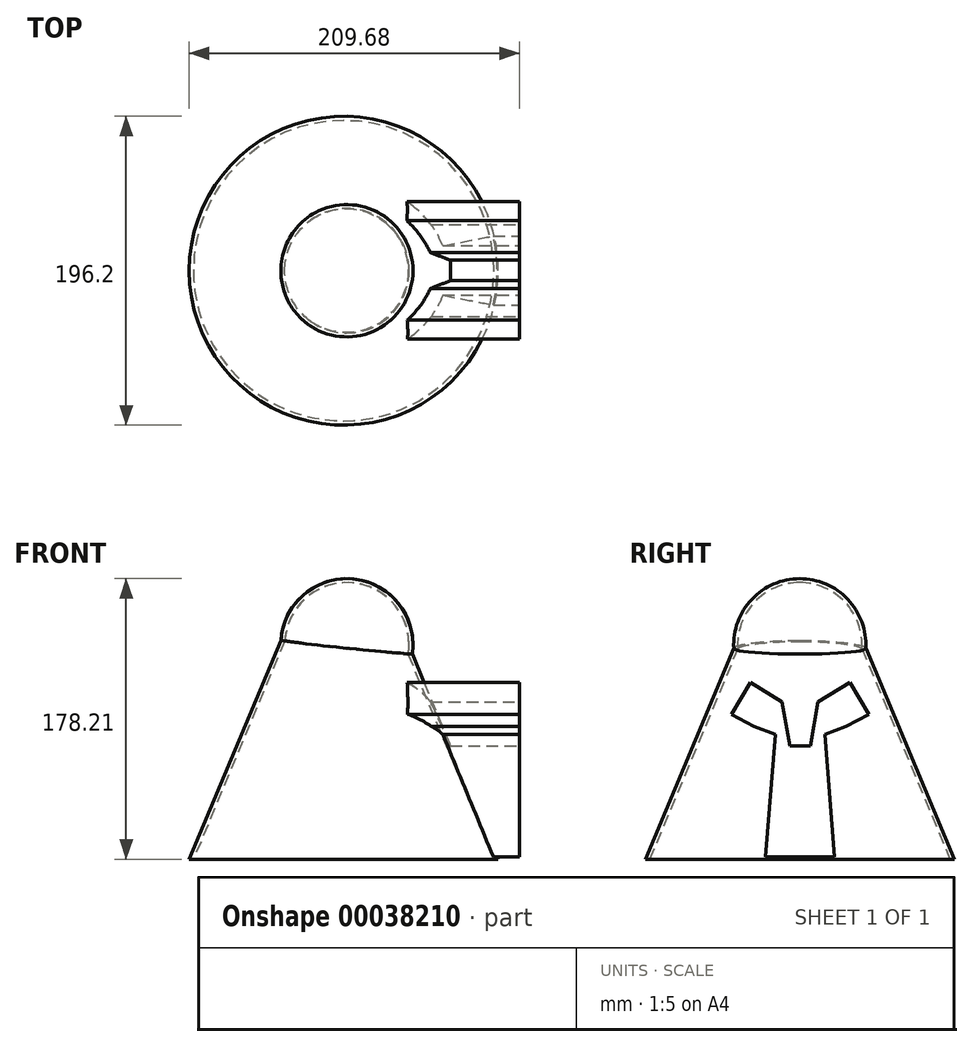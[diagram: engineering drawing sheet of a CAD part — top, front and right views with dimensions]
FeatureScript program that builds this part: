
annotation { "Feature Type Name" : "Feature", "Feature Type Description" : "" }
export const myFeature = defineFeature(function(context is Context, id is Id, definition is map)
    precondition{}
    {
        {
            var Q0;
            Q0=qCreatedBy(makeId("Front.planeOp"),FACE);
            var sketch = newSketch(context, id + "F0", { "sketchPlane" : qUnion([Q0])});
            skLineSegment(sketch, "E0", {"start": v(-51.63, 23.51) * mm, "end": v(55.11, 23.51) * mm});
            skCircle(sketch, "E1", {"center": v(-9.58, 23.51) * mm, "radius": 42 * mm});
            skSolve(sketch);
        }
        {
            var Q0;
            {var subQ0=sQuery(id+"F0.wireOp",EDGE,"E1");var subQ1=sQuery(id+"F0.wireOp",EDGE,"E0");var subQ3=makeQuery(id+"F0.imprint","INTERSECT",VERTEX,{"disambiguationData":[OD(0.0)],"derivedFrom":[subQ1,subQ0]});Q0=makeQuery(id+"F0.imprint","IMPRINT",FACE,{"disambiguationData":[TD([[makeQuery(id+"F0.imprint","IMPRINT",EDGE,{"disambiguationData":[TD([[subQ3,-1.0]])],"derivedFrom":subQ1}),1.0]])]});}
            var Q1;
            Q1=sQuery(id+"F0.wireOp",EDGE,"E0");
            revolve(context, id + "F1", {"entities" : qUnion([Q0]), "axis" : qUnion([Q1]), "revolveType" : RevolveType.FULL});
        }
        {
            var Q0;
            Q0=qCreatedBy(makeId("Front.planeOp"),FACE);
            var sketch = newSketch(context, id + "F2", { "sketchPlane" : qUnion([Q0])});
            skLineSegment(sketch, "E2", {"start": v(-11.58, 67.14) * mm, "end": v(-11.58, -112.7) * mm, "construction": true});
            skLineSegment(sketch, "E3", {"start": v(-11.58, 67.14) * mm, "end": v(-11.58, -112.7) * mm});
            skLineSegment(sketch, "E4", {"start": v(-11.58, -112.7) * mm, "end": v(-109.68, -112.7) * mm});
            skLineSegment(sketch, "E5", {"start": v(-109.68, -112.7) * mm, "end": v(-51.43, 26.45) * mm});
            skLineSegment(sketch, "E6", {"start": v(-51.43, 26.45) * mm, "end": v(-11.58, 64.48) * mm});
            skLineSegment(sketch, "E7", {"start": v(-84.12, 26.45) * mm, "end": v(51, 26.45) * mm});
            skSolve(sketch);
        }
        {
            var Q0;
            {var subQ1=sQuery(id+"F2.wireOp",EDGE,"E4");Q0=makeQuery(id+"F2.imprint","IMPRINT",FACE,{"disambiguationData":[TD([[makeQuery(id+"F2.imprint","IMPRINT",EDGE,{"derivedFrom":subQ1}),-1.0]])]});}
            var Q1;
            Q1=sQuery(id+"F2.wireOp",EDGE,"E3");
            revolve(context, id + "F3", {"operationType" : NewBodyOperationType.ADD, "entities" : qUnion([Q0]), "axis" : qUnion([Q1]), "revolveType" : RevolveType.FULL});
        }
        {
            var Q0;
            Q0=makeQuery(id+"F3.opRevolve","SWEPT_FACE",FACE,{"disambiguationData":[OSD([sQuery(id+"F2.wireOp",EDGE,"E4")])]});
            var Q1;
            Q1=makeQuery(id+"F1.opRevolve","SWEPT_BODY",BODY,{"disambiguationData":[OSD([sQuery(id+"F0.wireOp",EDGE,"E0"),sQuery(id+"F0.wireOp",EDGE,"E1")])]});
            shell(context, id + "F4", {"entities" : qUnion([Q0]), "parts" : qUnion([Q1]), "thickness" : 2.5 * mm});
        }
        {
            var Q0;
            Q0=qCreatedBy(makeId("Right.planeOp"),FACE);
            cPlane(context, id + "F5", {"entities" : qUnion([Q0]), "cplaneType" : CPlaneType.OFFSET, "offset" : 100 * mm, "width" : 150 * mm, "height" : 150 * mm});
        }
        {
            var Q0;
            Q0=qCreatedBy(id+"F5.planeOp",FACE);
            var sketch = newSketch(context, id + "F6", { "sketchPlane" : qUnion([Q0])});
            skLineSegment(sketch, "E8", {"start": v(31.72, -0.5) * mm, "end": v(11.56, -12.69) * mm});
            skLineSegment(sketch, "E9", {"start": v(29.32, -28.27) * mm, "end": v(15.83, -33.43) * mm});
            skLineSegment(sketch, "E10", {"start": v(11.56, -12.69) * mm, "end": v(6.7, -40.7) * mm});
            skLineSegment(sketch, "E11.MirrorCS", {"start": v(-31.4, -0.5) * mm, "end": v(-11.25, -12.69) * mm});
            skLineSegment(sketch, "E12.MirrorCS", {"start": v(-11.25, -12.69) * mm, "end": v(-6.39, -40.7) * mm});
            skLineSegment(sketch, "E13.MirrorCS", {"start": v(-29.01, -28.27) * mm, "end": v(-15.52, -33.43) * mm});
            skLineSegment(sketch, "E14.MirrorCS", {"start": v(-6.39, -40.7) * mm, "end": v(0.16, -40.7) * mm});
            skLineSegment(sketch, "E15", {"start": v(6.7, -40.7) * mm, "end": v(0.16, -40.7) * mm});
            skLineSegment(sketch, "E16", {"start": v(15.83, -33.43) * mm, "end": v(22.08, -111.23) * mm});
            skLineSegment(sketch, "E17.MirrorCS", {"start": v(-15.52, -33.43) * mm, "end": v(-21.77, -111.23) * mm});
            skLineSegment(sketch, "E18", {"start": v(31.72, -0.5) * mm, "end": v(43.85, -20.56) * mm});
            skLineSegment(sketch, "E19", {"start": v(43.85, -20.56) * mm, "end": v(29.32, -28.27) * mm});
            skLineSegment(sketch, "E20.MirrorCS", {"start": v(-31.4, -0.5) * mm, "end": v(-43.54, -20.56) * mm});
            skLineSegment(sketch, "E21.MirrorCS", {"start": v(-43.54, -20.56) * mm, "end": v(-29.01, -28.27) * mm});
            skLineSegment(sketch, "E22", {"start": v(-21.77, -111.23) * mm, "end": v(22.08, -111.23) * mm});
            skSolve(sketch);
        }
        {
            var Q0;
            Q0=makeQuery(id+"F6.imprint","IMPRINT",FACE,{"disambiguationData":[TD([[makeQuery(id+"F6.imprint","IMPRINT",EDGE,{"derivedFrom":sQuery(id+"F6.wireOp",EDGE,"E8")}),1.0]])]});
            var Q1;
            Q1=makeQuery(id+"F3.opRevolve","SWEPT_FACE",FACE,{"disambiguationData":[OSD([sQuery(id+"F2.wireOp",EDGE,"E5")])]});
            extrude(context, id + "F7", {"entities" : qUnion([Q0]), "operationType" : NewBodyOperationType.ADD, "endBound" : BoundingType.UP_TO_NEXT, "oppositeDirection" : true, "endBoundEntityFace" : qUnion([Q1]), "depth" : 25 * mm});
        }
    });
